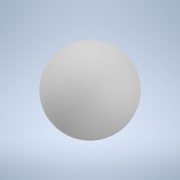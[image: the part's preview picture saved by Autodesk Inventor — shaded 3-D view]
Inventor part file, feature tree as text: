
AUTODESK INVENTOR PART (.ipt)
format: ipt  version: 2021 (Build 250183000, 183)  size: 126,464 bytes
history: native  units: in
note: dims shown in document units (in); Inventor stores cm internally (conversion verified against a paired STEP export)
features: revolve x1, sketch x1
ambient origin geometry x8: Origin, YZ Plane, XZ Plane, XY Plane, X Axis, Y Axis, Z Axis, Center Point
bodies: Solid1 (feature_tree)
feature tree (2):
  revolve  "Revolution1"  Angle=90.0deg
  sketch  "Sketch3"  dims[d1=11.811in d2=90.0deg]
